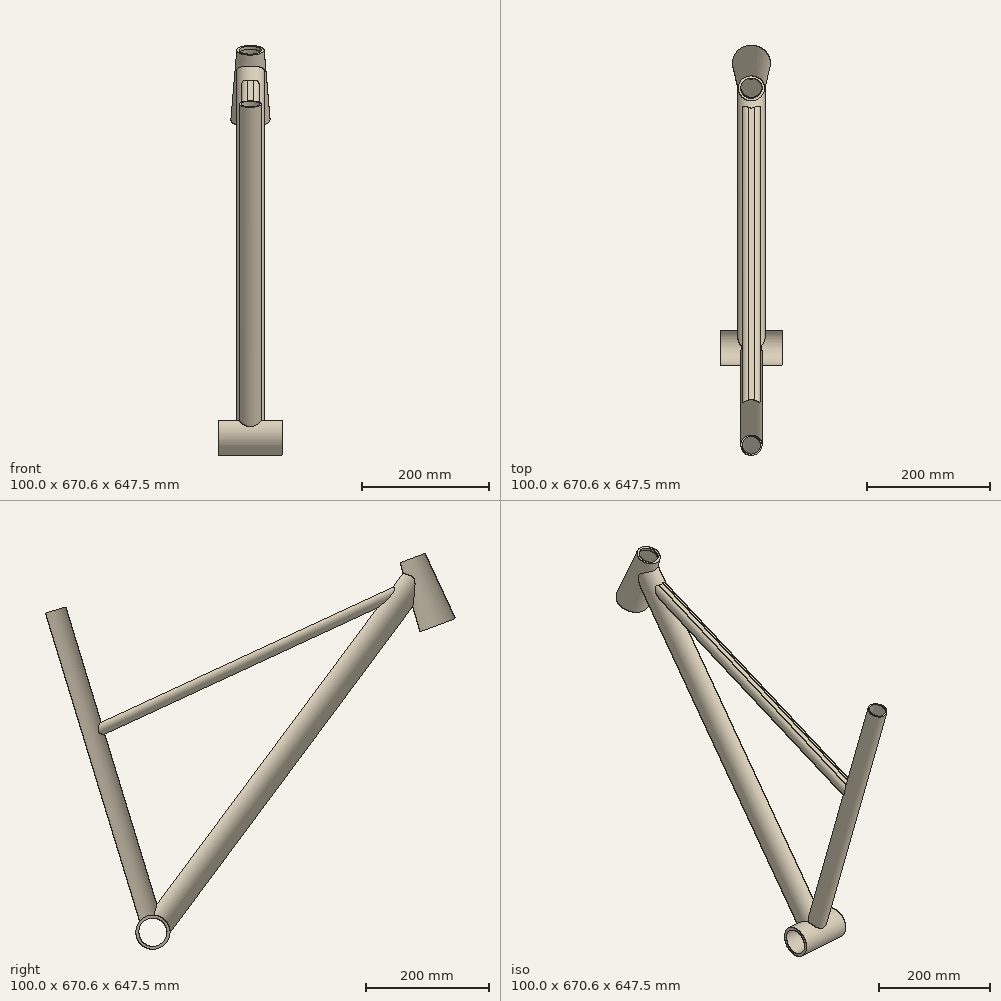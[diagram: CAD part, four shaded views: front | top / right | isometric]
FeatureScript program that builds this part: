
annotation { "Feature Type Name" : "Feature", "Feature Type Description" : "" }
export const myFeature = defineFeature(function(context is Context, id is Id, definition is map)
    precondition{}
    {
        {
            var Q0;
            Q0=qCreatedBy(makeId("Right.planeOp"),FACE);
            var sketch = newSketch(context, id + "F0", { "sketchPlane" : qUnion([Q0])});
            skLineSegment(sketch, "E0", {"start": v(0, 0) * mm, "end": v(-83.68, 223.8) * mm, "construction": true});
            skLineSegment(sketch, "E1", {"start": v(-295.85, 645.65) * mm, "end": v(-16.13, -102.49) * mm, "construction": true});
            skPoint(sketch, "E2", {"position": v(-219.37, 441.1) * mm});
            skLineSegment(sketch, "E3", {"start": v(-285.85, 416.25) * mm, "end": v(-152.9, 465.96) * mm, "construction": true});
            skCircle(sketch, "E4", {"center": v(0, -8.13) * mm, "radius": 375.7 * mm, "construction": true});
            skPoint(sketch, "E5", {"position": v(-260.46, 551) * mm});
            skPoint(sketch, "E6", {"position": v(-683.46, -60) * mm});
            skPoint(sketch, "E7", {"position": v(-1124.4, 0) * mm});
            skLineSegment(sketch, "E8", {"start": v(-1124.4, 0) * mm, "end": v(0, 0) * mm, "construction": true});
            skCircle(sketch, "E9", {"center": v(-1124.4, 0) * mm, "radius": 375.7 * mm, "construction": true});
            skLineSegment(sketch, "E10", {"start": v(-683.46, -60) * mm, "end": v(-904.4, 662.68) * mm, "construction": true});
            skLineSegment(sketch, "E11", {"start": v(-260.46, 551) * mm, "end": v(-947.84, 551) * mm, "construction": true});
            skPoint(sketch, "E12", {"position": v(-870.26, 551) * mm});
            skLineSegment(sketch, "E13", {"start": v(-207.61, 570.76) * mm, "end": v(-313.3, 531.24) * mm, "construction": true});
            skPoint(sketch, "E14", {"position": v(-249.95, 522.9) * mm});
            skLineSegment(sketch, "E15", {"start": v(-683.46, -60) * mm, "end": v(-249.95, 522.9) * mm, "construction": true});
            skPoint(sketch, "E16", {"position": v(-785.79, 274.7) * mm});
            skLineSegment(sketch, "E17", {"start": v(-785.79, 274.7) * mm, "end": v(-249.95, 522.9) * mm, "construction": true});
            skPoint(sketch, "E18", {"position": v(-466.7, 231.45) * mm});
            skPoint(sketch, "E19", {"position": v(-517.87, 398.8) * mm});
            skSolve(sketch);
        }
        {
            var Q0;
            Q0=qCreatedBy(makeId("Right.planeOp"),FACE);
            var sketch = newSketch(context, id + "F1", { "sketchPlane" : qUnion([Q0])});
            skLineSegment(sketch, "E20", {"start": v(-243.73, 432) * mm, "end": v(-245.48, 436.69) * mm});
            skLineSegment(sketch, "E21", {"start": v(-275.1, 540.19) * mm, "end": v(-245.48, 436.69) * mm});
            skLineSegment(sketch, "E22", {"start": v(-275.1, 540.19) * mm, "end": v(-276.85, 544.87) * mm});
            skLineSegment(sketch, "E23", {"start": v(-276.85, 544.87) * mm, "end": v(-280.8, 543.4) * mm});
            skLineSegment(sketch, "E24", {"start": v(-280.8, 543.4) * mm, "end": v(-248.4, 430.25) * mm});
            skLineSegment(sketch, "E25", {"start": v(-248.4, 430.25) * mm, "end": v(-243.73, 432) * mm});
            skSolve(sketch);
        }
        {
            var Q0;
            Q0 = qSketchRegion(id + "F1", true);
            var Q1;
            Q1=sQuery(id+"F0.wireOp",EDGE,"E1");
            revolve(context, id + "F2", {"entities" : qUnion([Q0]), "axis" : qUnion([Q1]), "revolveType" : RevolveType.FULL});
        }
        {
            var Q0;
            Q0=qCreatedBy(makeId("Right.planeOp"),FACE);
            var sketch = newSketch(context, id + "F3", { "sketchPlane" : qUnion([Q0])});
            skCircle(sketch, "E26", {"center": v(-685.15, -60.91) * mm, "radius": 23 * mm});
            skCircle(sketch, "E27", {"center": v(-685.15, -60.91) * mm, "radius": 28 * mm});
            skSolve(sketch);
        }
        {
            var Q0;
            Q0 = qSketchRegion(id + "F3", true);
            extrude(context, id + "F4", {"entities" : qUnion([Q0]), "endBound" : BoundingType.SYMMETRIC, "depth" : 100 * mm});
        }
        {
            var Q0;
            Q0=sQuery(id+"F0.wireOp",EDGE,"E10");
            var Q1;
            Q1=sQuery(id+"F0.wireOp",VERTEX,"E16");
            cPlane(context, id + "F5", {"entities" : qUnion([Q0, Q1]), "cplaneType" : CPlaneType.LINE_POINT, "offset" : 25 * mm, "width" : 150 * mm, "height" : 150 * mm});
        }
        {
            var Q0;
            Q0=qCreatedBy(id+"F5.planeOp",FACE);
            var sketch = newSketch(context, id + "F6", { "sketchPlane" : qUnion([Q0])});
            skCircle(sketch, "E28", {"center": v(0, -671.14) * mm, "radius": 17.4 * mm});
            skCircle(sketch, "E29", {"center": v(0, -671.14) * mm, "radius": 14.9 * mm});
            skSolve(sketch);
        }
        {
            var Q0;
            Q0 = qSketchRegion(id + "F6", true);
            var Q1;
            Q1=makeQuery(id+"F4.opExtrude","SWEPT_BODY",BODY,{"disambiguationData":[OSD([sQuery(id+"F3.wireOp",EDGE,"E26"),sQuery(id+"F3.wireOp",EDGE,"E27")])]});
            extrude(context, id + "F7", {"entities" : qUnion([Q0]), "endBound" : BoundingType.UP_TO_BODY, "oppositeDirection" : true, "endBoundEntityBody" : qUnion([Q1]), "depth" : 25 * mm, "hasSecondDirection" : true, "secondDirectionOppositeDirection" : false, "secondDirectionDepth" : 200 * mm});
        }
        {
            var Q0;
            Q0=sQuery(id+"F0.wireOp",EDGE,"E17");
            var Q1;
            Q1=sQuery(id+"F0.wireOp",VERTEX,"E19");
            cPlane(context, id + "F8", {"entities" : qUnion([Q0, Q1]), "cplaneType" : CPlaneType.LINE_POINT, "offset" : 25 * mm, "width" : 150 * mm, "height" : 150 * mm});
        }
        {
            var Q0;
            Q0=qCreatedBy(id+"F8.planeOp",FACE);
            var sketch = newSketch(context, id + "F9", { "sketchPlane" : qUnion([Q0])});
            skLineSegment(sketch, "E30", {"start": v(-5, 579.53) * mm, "end": v(5, 579.53) * mm});
            skLineSegment(sketch, "E31", {"start": v(-5, 559.53) * mm, "end": v(5, 559.53) * mm});
            skArc(sketch, "E32", {"start": v(-5, 579.53) * mm, "mid": v(-15, 569.53) * mm, "end": v(-5, 559.53) * mm});
            skArc(sketch, "E33", {"start": v(5, 559.53) * mm, "mid": v(15, 569.53) * mm, "end": v(5, 579.53) * mm});
            skLineSegment(sketch, "E34", {"start": v(5, 577.53) * mm, "end": v(-5, 577.53) * mm});
            skLineSegment(sketch, "E35", {"start": v(-5, 561.53) * mm, "end": v(5, 561.53) * mm});
            skArc(sketch, "E36", {"start": v(-5, 577.53) * mm, "mid": v(-13, 569.53) * mm, "end": v(-5, 561.53) * mm});
            skArc(sketch, "E37", {"start": v(5, 561.53) * mm, "mid": v(13, 569.53) * mm, "end": v(5, 577.53) * mm});
            skSolve(sketch);
        }
        {
            var Q0;
            Q0 = qSketchRegion(id + "F9", true);
            var Q1;
            Q1=makeQuery(id+"F2.opRevolve","SWEPT_BODY",BODY,{"disambiguationData":[OSD([sQuery(id+"F1.wireOp",EDGE,"E20"),sQuery(id+"F1.wireOp",EDGE,"E21"),sQuery(id+"F1.wireOp",EDGE,"E22"),sQuery(id+"F1.wireOp",EDGE,"E23"),sQuery(id+"F1.wireOp",EDGE,"E24"),sQuery(id+"F1.wireOp",EDGE,"E25")])]});
            var Q2;
            Q2=makeQuery(id+"F7.opExtrude","SWEPT_BODY",BODY,{"disambiguationData":[OSD([sQuery(id+"F6.wireOp",EDGE,"E28"),sQuery(id+"F6.wireOp",EDGE,"E29")])]});
            extrude(context, id + "F10", {"entities" : qUnion([Q0]), "endBound" : BoundingType.UP_TO_BODY, "endBoundEntityBody" : qUnion([Q1]), "depth" : 25 * mm, "hasSecondDirection" : true, "secondDirectionBound" : SecondDirectionBoundingType.UP_TO_BODY, "secondDirectionOppositeDirection" : true, "secondDirectionBoundEntityBody" : qUnion([Q2]), "secondDirectionDepth" : 25 * mm});
        }
        {
            var Q0;
            Q0=sQuery(id+"F0.wireOp",EDGE,"E15");
            cPoint(context, id + "F11", {"entities" : qUnion([Q0]), "parameter" : 0.5});
        }
        {
            var Q0;
            Q0=sQuery(id+"F0.wireOp",EDGE,"E15");
            var Q1;
            Q1 = qCreatedBy(id + "F11" ,VERTEX);
            cPlane(context, id + "F12", {"entities" : qUnion([Q0, Q1]), "cplaneType" : CPlaneType.LINE_POINT, "offset" : 25 * mm, "width" : 150 * mm, "height" : 150 * mm});
        }
        {
            var Q0;
            Q0=qCreatedBy(id+"F12.planeOp",FACE);
            var sketch = newSketch(context, id + "F13", { "sketchPlane" : qUnion([Q0])});
            skCircle(sketch, "E38", {"center": v(0, -512.61) * mm, "radius": 20 * mm});
            skCircle(sketch, "E39", {"center": v(0, -512.61) * mm, "radius": 22.5 * mm});
            skSolve(sketch);
        }
        {
            var Q0;
            Q0 = qSketchRegion(id + "F13", true);
            var Q1;
            Q1=makeQuery(id+"F4.opExtrude","SWEPT_BODY",BODY,{"disambiguationData":[OSD([sQuery(id+"F3.wireOp",EDGE,"E26"),sQuery(id+"F3.wireOp",EDGE,"E27")])]});
            var Q2;
            Q2=makeQuery(id+"F2.opRevolve","SWEPT_FACE",FACE,{"disambiguationData":[OSD([sQuery(id+"F1.wireOp",EDGE,"E24")])]});
            var Q3;
            Q3=makeQuery(id+"F2.opRevolve","SWEPT_BODY",BODY,{"disambiguationData":[OSD([sQuery(id+"F1.wireOp",EDGE,"E20"),sQuery(id+"F1.wireOp",EDGE,"E21"),sQuery(id+"F1.wireOp",EDGE,"E22"),sQuery(id+"F1.wireOp",EDGE,"E23"),sQuery(id+"F1.wireOp",EDGE,"E24"),sQuery(id+"F1.wireOp",EDGE,"E25")])]});
            var Q4;
            Q4=sQuery(id+"F0.wireOp",VERTEX,"E14");
            extrude(context, id + "F14", {"entities" : qUnion([Q0]), "endBound" : BoundingType.UP_TO_BODY, "oppositeDirection" : true, "endBoundEntityBody" : qUnion([Q1]), "depth" : 25 * mm, "hasSecondDirection" : true, "secondDirectionBound" : SecondDirectionBoundingType.UP_TO_BODY, "secondDirectionOppositeDirection" : false, "secondDirectionBoundEntityFace" : qUnion([Q2]), "secondDirectionBoundEntityBody" : qUnion([Q3]), "secondDirectionBoundEntityVertex" : qUnion([Q4]), "secondDirectionDepth" : 25 * mm});
        }
    });
